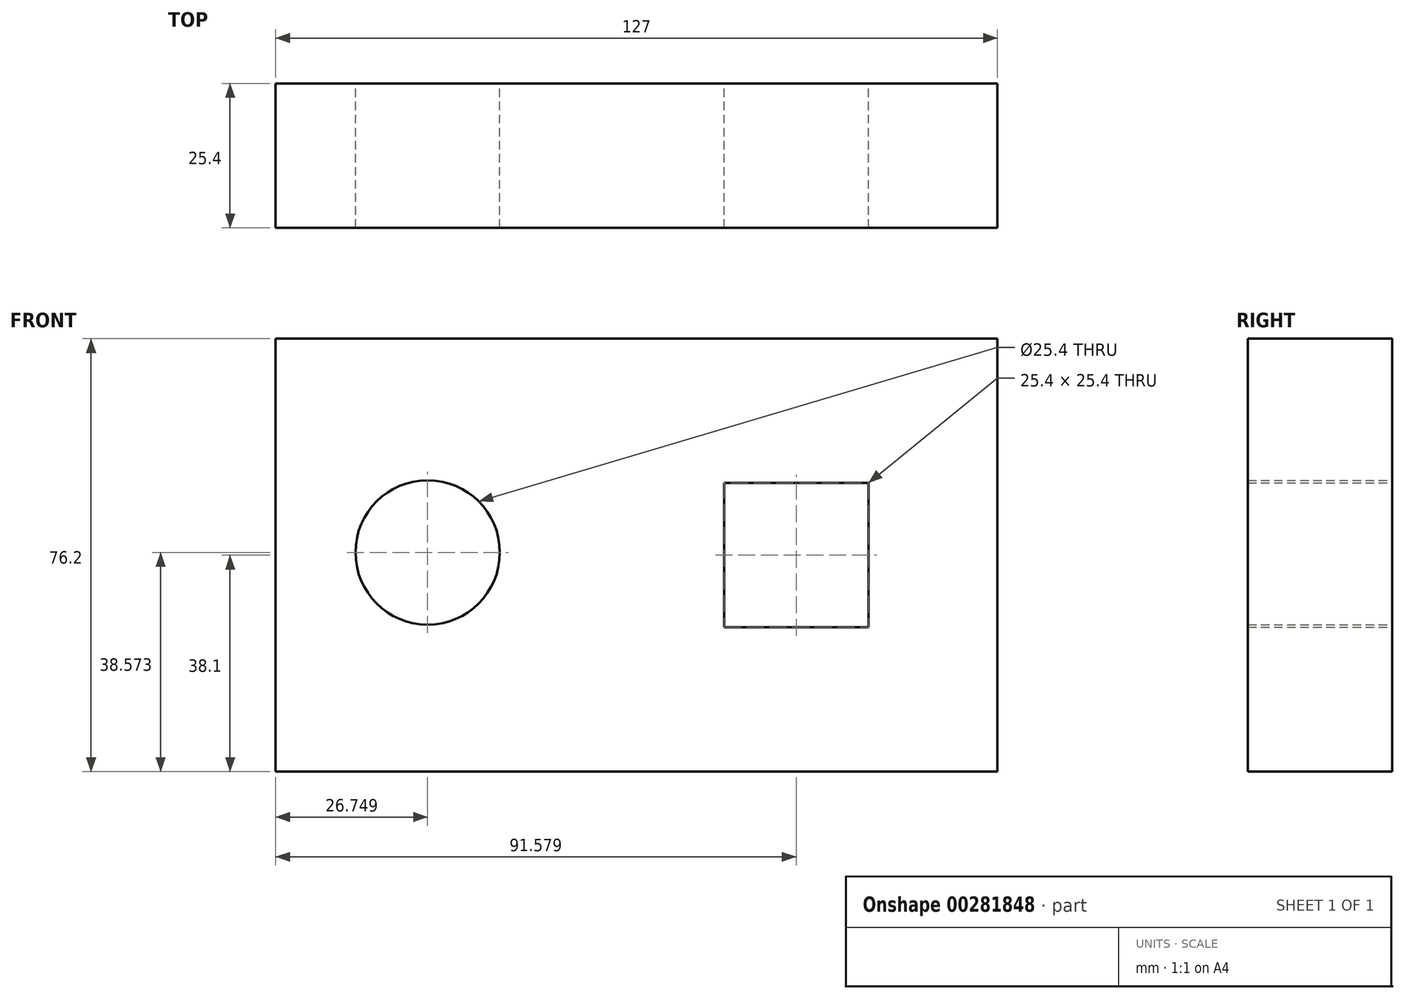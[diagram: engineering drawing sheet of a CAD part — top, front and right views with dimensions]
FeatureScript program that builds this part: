
annotation { "Feature Type Name" : "Feature", "Feature Type Description" : "" }
export const myFeature = defineFeature(function(context is Context, id is Id, definition is map)
    precondition{}
    {
        {
            var Q0;
            Q0=qCreatedBy(makeId("Front.planeOp"),FACE);
            var sketch = newSketch(context, id + "F0", { "sketchPlane" : qUnion([Q0])});
            skLineSegment(sketch, "E0.bottom", {"start": v(0, 0) * mm, "end": v(-127, 0) * mm});
            skLineSegment(sketch, "E0.top", {"start": v(0, 76.2) * mm, "end": v(-127, 76.2) * mm});
            skLineSegment(sketch, "E0.left", {"start": v(0, 0) * mm, "end": v(0, 76.2) * mm});
            skLineSegment(sketch, "E0.right", {"start": v(-127, 0) * mm, "end": v(-127, 76.2) * mm});
            skCircle(sketch, "E1", {"center": v(-100.25, 38.57) * mm, "radius": 12.7 * mm});
            skLineSegment(sketch, "E2.bottom", {"start": v(-22.72, 25.4) * mm, "end": v(-48.12, 25.4) * mm});
            skLineSegment(sketch, "E2.top", {"start": v(-22.72, 50.8) * mm, "end": v(-48.12, 50.8) * mm});
            skLineSegment(sketch, "E2.left", {"start": v(-22.72, 25.4) * mm, "end": v(-22.72, 50.8) * mm});
            skLineSegment(sketch, "E2.right", {"start": v(-48.12, 25.4) * mm, "end": v(-48.12, 50.8) * mm});
            skSolve(sketch);
        }
        {
            var Q0;
            Q0 = qSketchRegion(id + "F0", true);
            extrude(context, id + "F1", {"entities" : qUnion([Q0]), "depth" : 25.4 * mm});
        }
        {
            var Q0;
            Q0 = qSketchRegion(id + "F0", true);
            extrude(context, id + "F2", {"entities" : qUnion([Q0]), "operationType" : NewBodyOperationType.ADD, "depth" : 19.05 * mm});
        }
    });
